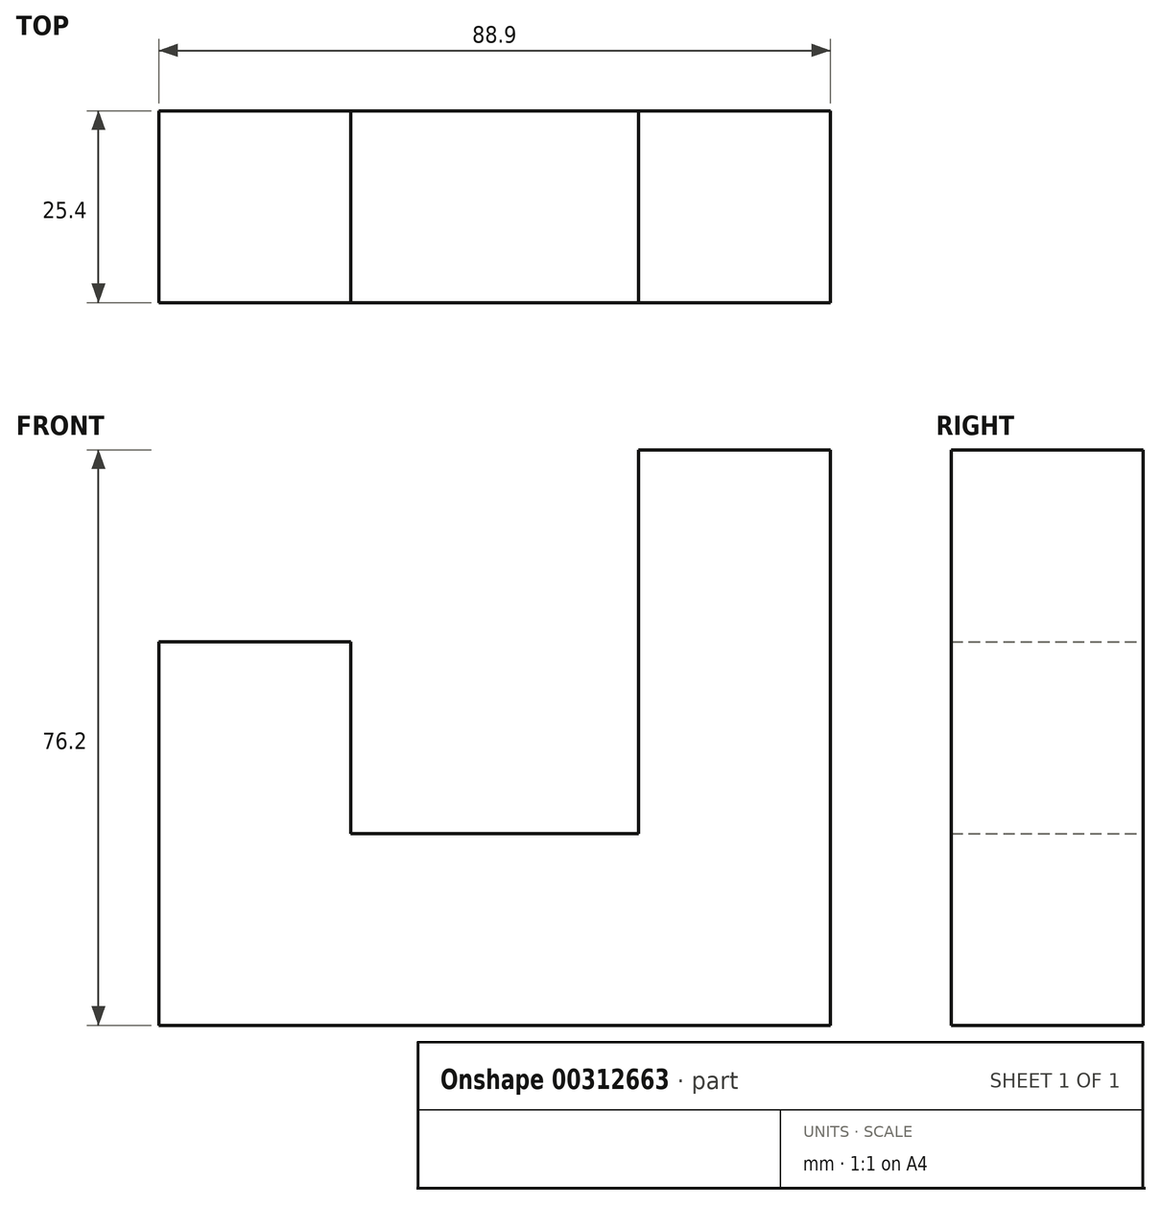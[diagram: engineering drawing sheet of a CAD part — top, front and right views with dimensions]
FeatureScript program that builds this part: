
annotation { "Feature Type Name" : "Feature", "Feature Type Description" : "" }
export const myFeature = defineFeature(function(context is Context, id is Id, definition is map)
    precondition{}
    {
        {
            var Q0;
            Q0=qCreatedBy(makeId("Front.planeOp"),FACE);
            var sketch = newSketch(context, id + "F0", { "sketchPlane" : qUnion([Q0])});
            skLineSegment(sketch, "E0", {"start": v(45.93, -44.75) * mm, "end": v(45.93, 31.45) * mm});
            skLineSegment(sketch, "E1", {"start": v(45.93, 31.45) * mm, "end": v(20.53, 31.45) * mm});
            skLineSegment(sketch, "E2", {"start": v(20.53, 31.45) * mm, "end": v(20.53, -19.35) * mm});
            skLineSegment(sketch, "E3", {"start": v(-17.57, 6.05) * mm, "end": v(-42.97, 6.05) * mm});
            skLineSegment(sketch, "E4", {"start": v(-42.97, -44.75) * mm, "end": v(45.93, -44.75) * mm});
            skLineSegment(sketch, "E5", {"start": v(-17.57, 6.05) * mm, "end": v(-17.57, -19.35) * mm});
            skLineSegment(sketch, "E6", {"start": v(20.53, -19.35) * mm, "end": v(-17.57, -19.35) * mm});
            skLineSegment(sketch, "E7", {"start": v(-42.97, 6.05) * mm, "end": v(-42.97, -44.75) * mm});
            skSolve(sketch);
        }
        {
            var Q0;
            Q0 = qSketchRegion(id + "F0", true);
            extrude(context, id + "F1", {"entities" : qUnion([Q0]), "depth" : 25.4 * mm});
        }
    });
